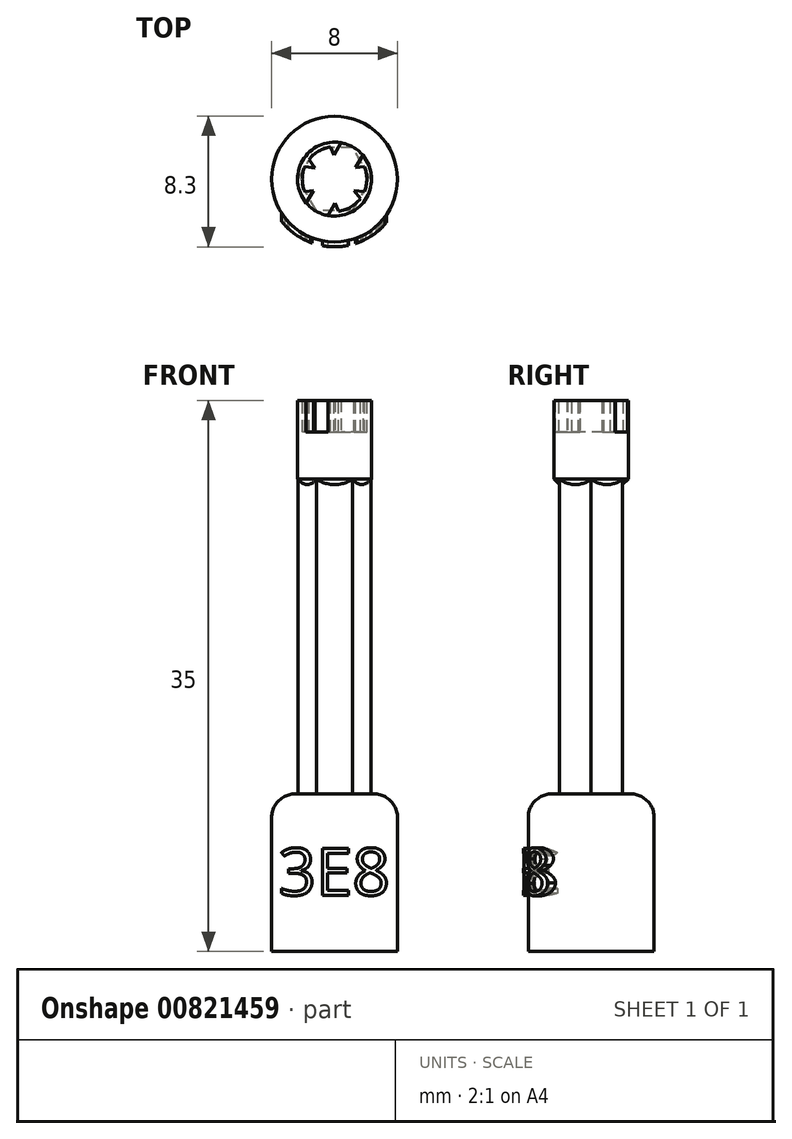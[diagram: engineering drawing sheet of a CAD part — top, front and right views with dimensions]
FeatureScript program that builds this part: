
annotation { "Feature Type Name" : "Feature", "Feature Type Description" : "" }
export const myFeature = defineFeature(function(context is Context, id is Id, definition is map)
    precondition{}
    {
        {
            assignVariable(context, id + "F0", {"name" : "bitlength", "anyValue" : 30});
        }
        {
            assignVariable(context, id + "F1", {"name" : "bitdepth", "anyValue" : 5});
        }
        {
            assignVariable(context, id + "F2", {"name" : "socketdepth", "anyValue" : 2});
        }
        {
            var Q0;
            Q0=qCreatedBy(makeId("Top.planeOp"),FACE);
            var sketch = newSketch(context, id + "F3", { "sketchPlane" : qUnion([Q0])});
            skLineSegment(sketch, "E0", {"start": v(0, 2) * mm, "end": v(0, -2) * mm, "construction": true});
            skLineSegment(sketch, "E1", {"start": v(-1.15, -2) * mm, "end": v(1.15, -2) * mm});
            skLineSegment(sketch, "E2", {"start": v(-1.15, 2) * mm, "end": v(1.15, 2) * mm});
            skLineSegment(sketch, "E3", {"start": v(1.15, 2) * mm, "end": v(2.3, 0) * mm});
            skLineSegment(sketch, "E4", {"start": v(2.3, 0) * mm, "end": v(1.15, -2) * mm});
            skLineSegment(sketch, "E5", {"start": v(-1.15, 2) * mm, "end": v(-2.3, 0) * mm});
            skLineSegment(sketch, "E6", {"start": v(-2.3, 0) * mm, "end": v(-1.15, -2) * mm});
            skLineSegment(sketch, "E7", {"start": v(-1.73, -1) * mm, "end": v(1.73, 1) * mm, "construction": true});
            skLineSegment(sketch, "E8", {"start": v(-1.73, 1) * mm, "end": v(1.73, -1) * mm, "construction": true});
            skSolve(sketch);
        }
        {
            var Q0;
            Q0=makeQuery(id+"F3.imprint","IMPRINT",FACE,{"disambiguationData":[TD([[makeQuery(id+"F3.imprint","IMPRINT",EDGE,{"derivedFrom":sQuery(id+"F3.wireOp",EDGE,"E1")}),1.0]])]});
            extrude(context, id + "F4", {"entities" : qUnion([Q0]), "depth" : (getVariable(context, 'bitlength')) * mm, "offsetDistance" : 25 * mm});
        }
        {
            var Q0;
            Q0=makeQuery(id+"F4.opExtrude","CAP_FACE",FACE,{"disambiguationData":[OSD([sQuery(id+"F3.wireOp",EDGE,"E1"),sQuery(id+"F3.wireOp",EDGE,"E2"),sQuery(id+"F3.wireOp",EDGE,"E3"),sQuery(id+"F3.wireOp",EDGE,"E4"),sQuery(id+"F3.wireOp",EDGE,"E5"),sQuery(id+"F3.wireOp",EDGE,"E6")])],"isStart":false});
            var sketch = newSketch(context, id + "F5", { "sketchPlane" : qUnion([Q0])});
            skCircle(sketch, "E9", {"center": v(0, 0) * mm, "radius": 2.35 * mm});
            skSolve(sketch);
        }
        {
            var Q0;
            Q0 = qSketchRegion(id + "F5", true);
            extrude(context, id + "F6", {"entities" : qUnion([Q0]), "operationType" : NewBodyOperationType.ADD, "depth" : (getVariable(context, 'bitdepth')) * mm, "offsetDistance" : 25 * mm});
        }
        {
            var Q0;
            Q0=makeQuery(id+"F6.opExtrude","CAP_FACE",FACE,{"disambiguationData":[OSD([sQuery(id+"F5.wireOp",EDGE,"E9")])],"isStart":false});
            var sketch = newSketch(context, id + "F7", { "sketchPlane" : qUnion([Q0])});
            skCircle(sketch, "E10", {"center": v(0, 0) * mm, "radius": 2.05 * mm});
            skLineSegment(sketch, "E11", {"start": v(-0.25, 2.03) * mm, "end": v(0.25, 2.03) * mm, "construction": true});
            skLineSegment(sketch, "E12", {"start": v(-0.25, 2.03) * mm, "end": v(0, 1.43) * mm});
            skLineSegment(sketch, "E13", {"start": v(0, 1.43) * mm, "end": v(0.25, 2.03) * mm});
            skLineSegment(sketch, "E14.1.0", {"start": v(-1.89, 0.8) * mm, "end": v(-1.24, 0.72) * mm});
            skLineSegment(sketch, "E14.1.1", {"start": v(-1.24, 0.72) * mm, "end": v(-1.64, 1.23) * mm});
            skLineSegment(sketch, "E14.2.0", {"start": v(-1.64, -1.23) * mm, "end": v(-1.24, -0.72) * mm});
            skLineSegment(sketch, "E14.2.1", {"start": v(-1.24, -0.72) * mm, "end": v(-1.89, -0.8) * mm});
            skLineSegment(sketch, "E14.3.0", {"start": v(0.25, -2.03) * mm, "end": v(0, -1.43) * mm});
            skLineSegment(sketch, "E14.3.1", {"start": v(0, -1.43) * mm, "end": v(-0.25, -2.03) * mm});
            skLineSegment(sketch, "E14.4.0", {"start": v(1.89, -0.8) * mm, "end": v(1.24, -0.72) * mm});
            skLineSegment(sketch, "E14.4.1", {"start": v(1.24, -0.72) * mm, "end": v(1.64, -1.23) * mm});
            skLineSegment(sketch, "E14.5.0", {"start": v(1.64, 1.23) * mm, "end": v(1.24, 0.72) * mm});
            skLineSegment(sketch, "E14.5.1", {"start": v(1.24, 0.72) * mm, "end": v(1.89, 0.8) * mm});
            skSolve(sketch);
        }
        {
            var Q0;
            {var subQ7=sQuery(id+"F7.wireOp",EDGE,"E12");Q0=makeQuery(id+"F7.imprint","IMPRINT",FACE,{"disambiguationData":[TD([[makeQuery(id+"F7.imprint","IMPRINT",EDGE,{"derivedFrom":subQ7}),-1.0]])]});}
            extrude(context, id + "F8", {"entities" : qUnion([Q0]), "operationType" : NewBodyOperationType.REMOVE, "oppositeDirection" : true, "depth" : (getVariable(context, 'socketdepth')) * mm, "offsetDistance" : 25 * mm});
        }
        {
            var Q0;
            Q0=qCreatedBy(makeId("Right.planeOp"),FACE);
            var sketch = newSketch(context, id + "F9", { "sketchPlane" : qUnion([Q0])});
            skLineSegment(sketch, "E15", {"start": v(0, 30) * mm, "end": v(0, 0) * mm, "construction": true});
            skLineSegment(sketch, "E16.0", {"start": v(-2.35, 30) * mm, "end": v(2.35, 30) * mm, "construction": true});
            skLineSegment(sketch, "E17", {"start": v(-2.35, 30) * mm, "end": v(0, 27.65) * mm});
            skLineSegment(sketch, "E18", {"start": v(0, 27.65) * mm, "end": v(0, 30) * mm});
            skLineSegment(sketch, "E19", {"start": v(-2.35, 30) * mm, "end": v(0, 30) * mm});
            skSolve(sketch);
        }
        {
            var Q0;
            Q0=makeQuery(id+"F9.imprint","IMPRINT",FACE,{"disambiguationData":[TD([[makeQuery(id+"F9.imprint","IMPRINT",EDGE,{"derivedFrom":sQuery(id+"F9.wireOp",EDGE,"E17")}),1.0]])]});
            var Q1;
            Q1=sQuery(id+"F9.wireOp",EDGE,"E15");
            revolve(context, id + "F10", {"operationType" : NewBodyOperationType.ADD, "surfaceOperationType" : NewSurfaceOperationType.NEW, "entities" : qUnion([Q0]), "axis" : qUnion([Q1]), "revolveType" : RevolveType.FULL});
        }
        {
            var Q0;
            Q0=makeQuery(id+"F4.opExtrude","CAP_FACE",FACE,{"disambiguationData":[OSD([sQuery(id+"F3.wireOp",EDGE,"E1"),sQuery(id+"F3.wireOp",EDGE,"E2"),sQuery(id+"F3.wireOp",EDGE,"E3"),sQuery(id+"F3.wireOp",EDGE,"E4"),sQuery(id+"F3.wireOp",EDGE,"E5"),sQuery(id+"F3.wireOp",EDGE,"E6")])],"isStart":true});
            var sketch = newSketch(context, id + "F11", { "sketchPlane" : qUnion([Q0])});
            skCircle(sketch, "E20", {"center": v(0, 0) * mm, "radius": 4 * mm});
            skSolve(sketch);
        }
        {
            var Q0;
            Q0 = qSketchRegion(id + "F11", true);
            extrude(context, id + "F12", {"entities" : qUnion([Q0]), "operationType" : NewBodyOperationType.ADD, "oppositeDirection" : true, "depth" : 10 * mm, "offsetDistance" : 25 * mm});
        }
        {
            var Q0;
            Q0=makeQuery(id+"F12.opExtrude","CAP_EDGE",EDGE,{"disambiguationData":[OSD([sQuery(id+"F11.wireOp",EDGE,"E20")])],"isStart":false});
            fillet(context, id + "F13", {"entities" : qUnion([Q0]), "radius" : 1.5 * mm, "tangentPropagation" : true, "allowEdgeOverflow" : false});
        }
        {
            var Q0;
            Q0=makeQuery(id+"F8.boolean.opBoolean","COPY",VERTEX,{"derivedFrom":makeQuery(id+"F8.opExtrude","CAP_VERTEX",VERTEX,{"disambiguationData":[OSD([sQuery(id+"F7.wireOp",EDGE,"E10"),sQuery(id+"F7.wireOp",EDGE,"E13")])],"isStart":true})});
            var Q1;
            Q1=makeQuery(id+"F8.boolean.opBoolean","COPY",VERTEX,{"derivedFrom":makeQuery(id+"F8.opExtrude","CAP_VERTEX",VERTEX,{"disambiguationData":[OSD([sQuery(id+"F7.wireOp",EDGE,"E10"),sQuery(id+"F7.wireOp",EDGE,"E13")])],"isStart":false})});
            var Q2;
            Q2=makeQuery(id+"F8.boolean.opBoolean","COPY",VERTEX,{"derivedFrom":makeQuery(id+"F8.opExtrude","CAP_VERTEX",VERTEX,{"disambiguationData":[OSD([sQuery(id+"F7.wireOp",EDGE,"E10"),sQuery(id+"F7.wireOp",EDGE,"E14.5.0")])],"isStart":true})});
            cPlane(context, id + "F14", {"entities" : qUnion([Q0, Q1, Q2]), "cplaneType" : CPlaneType.THREE_POINT, "offset" : 25 * mm, "width" : 150 * mm, "height" : 150 * mm});
        }
        {
            var Q0;
            Q0=qCreatedBy(id+"F14.planeOp",FACE);
            var sketch = newSketch(context, id + "F15", { "sketchPlane" : qUnion([Q0])});
            skPoint(sketch, "E21.0", {"position": v(0.8, 35) * mm});
            skPoint(sketch, "E22.0", {"position": v(-0.8, 33) * mm});
            skLineSegment(sketch, "E23.bottom", {"start": v(0.8, 35) * mm, "end": v(-0.8, 35) * mm});
            skLineSegment(sketch, "E23.top", {"start": v(0.8, 33) * mm, "end": v(-0.8, 33) * mm});
            skLineSegment(sketch, "E23.left", {"start": v(0.8, 35) * mm, "end": v(0.8, 33) * mm});
            skLineSegment(sketch, "E23.right", {"start": v(-0.8, 35) * mm, "end": v(-0.8, 33) * mm});
            skSolve(sketch);
        }
        {
            var Q0;
            Q0 = qSketchRegion(id + "F15", true);
            extrude(context, id + "F16", {"entities" : qUnion([Q0]), "operationType" : NewBodyOperationType.REMOVE, "endBound" : BoundingType.THROUGH_ALL, "oppositeDirection" : true, "depth" : 25 * mm, "offsetDistance" : 25 * mm, "hasSecondDirection" : true, "secondDirectionBound" : SecondDirectionBoundingType.THROUGH_ALL, "secondDirectionOppositeDirection" : false, "secondDirectionDepth" : 25 * mm});
        }
        {
            var Q0;
            Q0=qCreatedBy(makeId("Front.planeOp"),FACE);
            cPlane(context, id + "F17", {"entities" : qUnion([Q0]), "cplaneType" : CPlaneType.OFFSET, "offset" : 5 * mm, "width" : 150 * mm, "height" : 150 * mm});
        }
        {
            var Q0;
            Q0=qCreatedBy(id+"F17.planeOp",FACE);
            var sketch = newSketch(context, id + "F18", { "sketchPlane" : qUnion([Q0])});
            skLineSegment(sketch, "E24", {"start": v(-4, 0.82) * mm, "end": v(-4, 8.5) * mm, "construction": true});
            skLineSegment(sketch, "E25", {"start": v(4, 9.32) * mm, "end": v(4, 0) * mm, "construction": true});
            skLineSegment(sketch, "E26", {"start": v(4, 9.32) * mm, "end": v(-4, 0.82) * mm, "construction": true});
            skText(sketch, "E27", { "text": "3E8", "fontName": "OpenSans-Regular.ttf"});
            skPoint(sketch, "E28", {"position": v(0, 5.07) * mm});
            const initialGuessF18  = {"E27": [-0.00357, 0.00357, 1, 0, 0.003]};
            skSetInitialGuess(sketch, initialGuessF18);
            skSolve(sketch);
        }
        {
            var Q0;
            Q0 = qSketchRegion(id + "F18", true);
            extrude(context, id + "F19", {"entities" : qUnion([Q0]), "operationType" : NewBodyOperationType.ADD, "endBound" : BoundingType.UP_TO_NEXT, "oppositeDirection" : true, "depth" : 25 * mm, "offsetDistance" : 25 * mm});
        }
        {
            var Q0;
            Q0=qCreatedBy(makeId("Front.planeOp"),FACE);
            var sketch = newSketch(context, id + "F20", { "sketchPlane" : qUnion([Q0])});
            skLineSegment(sketch, "E29", {"start": v(4, 8.5) * mm, "end": v(4, 0) * mm, "construction": true});
            skLineSegment(sketch, "E30", {"start": v(4.3, 8.5) * mm, "end": v(4.3, 0) * mm});
            skLineSegment(sketch, "E31", {"start": v(4.3, 0) * mm, "end": v(6.75, 0) * mm});
            skLineSegment(sketch, "E32", {"start": v(6.75, 0) * mm, "end": v(6.75, 8.5) * mm});
            skLineSegment(sketch, "E33", {"start": v(6.75, 8.5) * mm, "end": v(4.3, 8.5) * mm});
            skLineSegment(sketch, "E34", {"start": v(0, 0) * mm, "end": v(0, 4.56) * mm, "construction": true});
            skSolve(sketch);
        }
        {
            var Q0;
            Q0 = qSketchRegion(id + "F20", true);
            var Q1;
            Q1=sQuery(id+"F20.wireOp",EDGE,"E34");
            revolve(context, id + "F21", {"operationType" : NewBodyOperationType.REMOVE, "surfaceOperationType" : NewSurfaceOperationType.NEW, "entities" : qUnion([Q0]), "axis" : qUnion([Q1]), "revolveType" : RevolveType.FULL, "oppositeDirection" : true});
        }
    });
